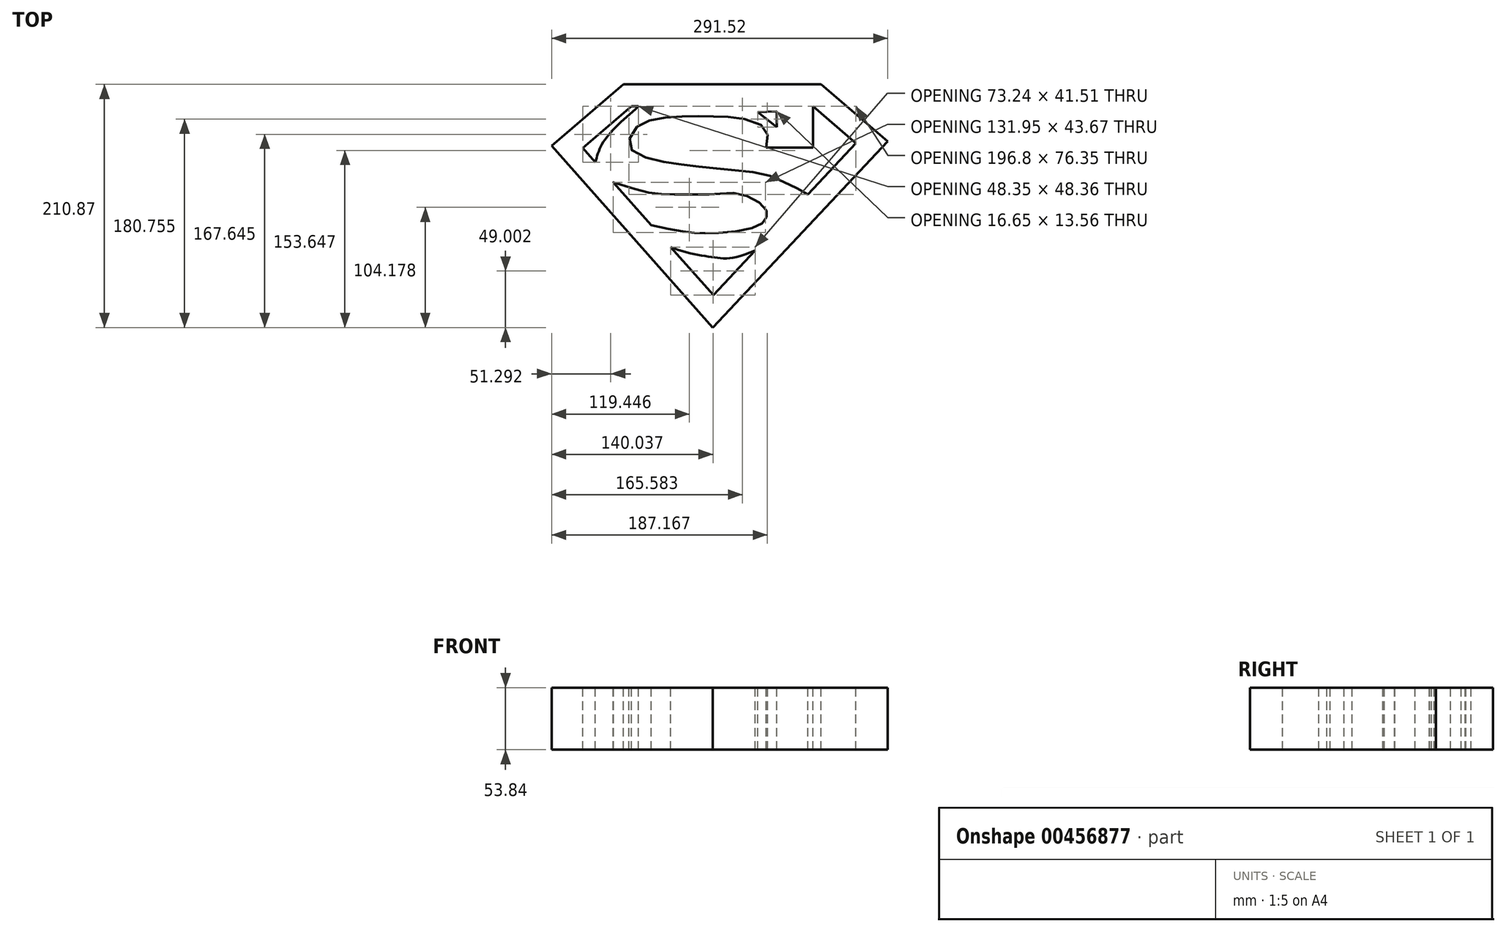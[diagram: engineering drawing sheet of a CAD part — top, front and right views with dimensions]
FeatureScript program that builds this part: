
annotation { "Feature Type Name" : "Feature", "Feature Type Description" : "" }
export const myFeature = defineFeature(function(context is Context, id is Id, definition is map)
    precondition{}
    {
        {
            var Q0;
            Q0=qCreatedBy(makeId("Top.planeOp"),FACE);
            var sketch = newSketch(context, id + "F0", { "sketchPlane" : qUnion([Q0])});
            skLineSegment(sketch, "E0", {"start": v(0, 76.35) * mm, "end": v(-71, 76.35) * mm});
            skLineSegment(sketch, "E1", {"start": v(-71, 76.35) * mm, "end": v(-113.15, 40.22) * mm});
            skLineSegment(sketch, "E2", {"start": v(-113.15, 40.22) * mm, "end": v(0, -87.22) * mm});
            skLineSegment(sketch, "E3.MirrorCS", {"start": v(0, 76.35) * mm, "end": v(86.52, 76.35) * mm});
            skLineSegment(sketch, "E4.MirrorCS", {"start": v(86.52, 76.35) * mm, "end": v(123.71, 44.47) * mm});
            skLineSegment(sketch, "E5.MirrorCS", {"start": v(123.71, 44.47) * mm, "end": v(0, -87.22) * mm});
            skLineSegment(sketch, "E6.0", {"start": v(0, 95.4) * mm, "end": v(-78.05, 95.4) * mm});
            skLineSegment(sketch, "E6.1", {"start": v(-140.27, 42.07) * mm, "end": v(-0.4, -115.47) * mm});
            skLineSegment(sketch, "E6.2", {"start": v(151.25, 45.96) * mm, "end": v(-0.4, -115.47) * mm});
            skLineSegment(sketch, "E6.3", {"start": v(-78.05, 95.4) * mm, "end": v(-140.27, 42.07) * mm});
            skLineSegment(sketch, "E6.4", {"start": v(93.57, 95.4) * mm, "end": v(151.25, 45.96) * mm});
            skLineSegment(sketch, "E6.5", {"start": v(0, 95.4) * mm, "end": v(93.57, 95.4) * mm});
            skLineSegment(sketch, "E7", {"start": v(86.52, 76.35) * mm, "end": v(86.52, 40.45) * mm});
            skLineSegment(sketch, "E8", {"start": v(86.52, 40.45) * mm, "end": v(45.93, 40.45) * mm});
            skFitSpline(sketch, "E9", {"points": [v(45.93, 40.45) * mm, v(46.29, 55.59) * mm, v(23.36, 65.97) * mm, v(0, 67.7) * mm, v(-23.8, 67.7) * mm, v(-51.48, 65.1) * mm, v(-68.78, 56.02) * mm, v(-72.24, 40.45) * mm, v(-49.75, 29.63) * mm, v(-18.17, 24.87) * mm, v(13.84, 21.41) * mm, v(45.42, 17.09) * mm, v(67.05, 8) * mm, v(81.94, 0) * mm], "startDerivative": vector(-11.2, 264.55) * mm, "endDerivative": vector(159.1, -138.94) * mm});
            skFitSpline(sketch, "E10", {"points": [v(36.39, -48.49) * mm, v(0, -54.58) * mm, v(-36.85, -45.71) * mm], "startDerivative": vector(-113.3, -50.63) * mm, "endDerivative": vector(-79.19, 32.58) * mm});
            skPoint(sketch, "E11.1.internal.snap0", {"position": v(-56.58, -23.5) * mm});
            skPoint(sketch, "E11.2.internal.snap0", {"position": v(-56.58, -23.5) * mm});
            skFitSpline(sketch, "E11", {"points": [v(-53.74, -26.7) * mm, v(-19.5, -32.9) * mm, v(0, -33.68) * mm, v(38.57, -27.48) * mm, v(45.93, -20.12) * mm, v(45.93, -13.54) * mm, v(25.4, 0) * mm, v(0, 0) * mm, v(-16.02, 0) * mm, v(-41.1, 0) * mm, v(-67.92, 4.54) * mm, v(-86.8, 10.54) * mm, v(-86.49, 10.2) * mm, v(-86.27, 9.95) * mm], "startDerivative": vector(367.2, -94.32) * mm, "endDerivative": vector(17.23, -23.54) * mm});
            skFitSpline(sketch, "E12", {"points": [v(-102.3, 28) * mm, v(-95, 46.1) * mm, v(-64.8, 76.35) * mm], "startDerivative": vector(11.52, 43.71) * mm, "endDerivative": vector(60.3, 52.44) * mm});
            skLineSegment(sketch, "E13", {"start": v(38.57, 71.29) * mm, "end": v(55.22, 58.5) * mm});
            skLineSegment(sketch, "E14", {"start": v(55.22, 58.5) * mm, "end": v(55.22, 72.06) * mm});
            skLineSegment(sketch, "E15", {"start": v(55.22, 72.06) * mm, "end": v(38.57, 71.29) * mm});
            skLineSegment(sketch, "E16", {"start": v(55.22, 58.5) * mm, "end": v(55.22, 65.28) * mm});
            skSolve(sketch);
        }
        {
            var Q0;
            {var subQ5=sQuery(id+"F0.wireOp",EDGE,"E3.MirrorCS");Q0=makeQuery(id+"F0.imprint","IMPRINT",FACE,{"disambiguationData":[TD([[makeQuery(id+"F0.imprint","IMPRINT",EDGE,{"derivedFrom":subQ5}),-1.0]])]});}
            var Q1;
            {var subQ15=sQuery(id+"F0.wireOp",EDGE,"E1");Q1=makeQuery(id+"F0.imprint","IMPRINT",FACE,{"disambiguationData":[TD([[makeQuery(id+"F0.imprint","IMPRINT",EDGE,{"derivedFrom":subQ15}),-1.0]])]});}
            extrude(context, id + "F1", {"entities" : qUnion([Q0, Q1]), "endBound" : BoundingType.SYMMETRIC, "oppositeDirection" : true, "depth" : 53.85 * mm});
        }
    });
